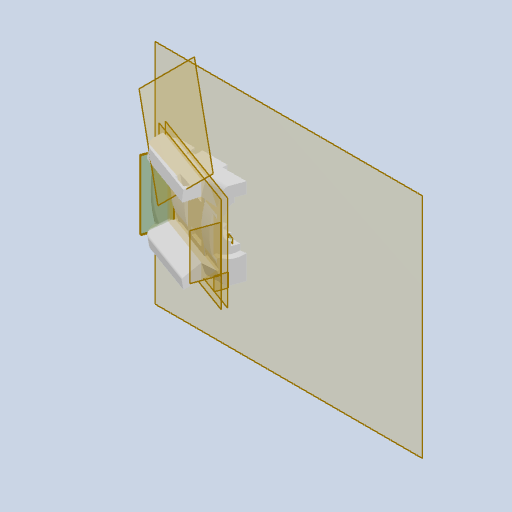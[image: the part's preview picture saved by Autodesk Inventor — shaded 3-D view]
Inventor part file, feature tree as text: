
AUTODESK INVENTOR PART (.ipt)
format: ipt  version: 2022 (Build 260153000, 153)  size: 1,060,352 bytes
history: native  units: mm
features: reference x50, other x25, extrude x24, sketch x23, projected_geometry x12, fillet x11, mirror x2, chamfer x2
ambient origin geometry x8: Origin, YZ Plane, XZ Plane, XY Plane, X Axis, Y Axis, Z Axis, Center Point
bodies: Body1 (feature_tree)
feature tree (149):
  other  "Твердое тело1"
  other  "РабПлоскость1"
  extrude  "Выдавливание1"  Depth=0.3mm
  other  "РабПлоскость2"
  extrude  "Выдавливание2"  Depth=0.3mm
  extrude  "Выдавливание3"  Depth=40.0mm TaperAngle=0.0deg
  other  "РабПлоскость3"
  extrude  "Выдавливание4"  Depth=0.5mm
  extrude  "Выдавливание5"  Depth=0.5mm
  mirror  "Зеркальное отражение1"
  other  "РабПлоскость4"
  extrude  "Выдавливание6"  Depth=0.5mm
  fillet  "Сопряжение1"  Radius=200.0mm
  extrude  "Выдавливание7"  Depth=200.0mm TaperAngle=0.0deg
  extrude  "Выдавливание8"  Depth=1.0mm
  other  "РабПлоскость5"
  extrude  "Выдавливание9"  Depth=10.0mm TaperAngle=0.0deg
  extrude  "Выдавливание10"  Depth=0.2mm
  other  "РабПлоскость6"
  extrude  "Выдавливание11"  Depth=0.2mm
  extrude  "Выдавливание12"  Depth=0.2mm
  chamfer  "Фаска1"  Distance=0.2mm
  extrude  "Выдавливание13"  Depth=17.85mm TaperAngle=0.0deg
  other  "РабПлоскость8"
  extrude  "Выдавливание14"  Depth=17.5mm TaperAngle=0.0deg
  extrude  "Выдавливание15"  Depth=1.675mm TaperAngle=0.0deg
  extrude  "Выдавливание16"  Depth=27.0mm
  fillet  "Сопряжение3"  Radius=1.5mm
  fillet  "Сопряжение4"  Radius=3.15mm
  fillet  "Сопряжение6"  Radius=0.3mm
  extrude  "Выдавливание17"  Depth=200.0mm TaperAngle=0.0deg
  extrude  "Выдавливание18"  Depth=0.4mm
  chamfer  "Фаска2"  Distance=0.4mm
  fillet  "Сопряжение7"  Radius=10.0mm
  extrude  "Выдавливание19"  Depth=1.25mm TaperAngle=0.0deg
  extrude  "Выдавливание20"  Depth=5.0mm TaperAngle=0.0deg
  fillet  "Сопряжение8"  Radius=0.8mm
  fillet  "Сопряжение9"  Radius=10.0mm
  other  "РабПлоскость9"
  extrude  "Выдавливание21"  Depth=5.0mm TaperAngle=0.0deg
  extrude  "Выдавливание22"  Depth=10.0mm TaperAngle=0.0deg
  fillet  "Сопряжение10"  Radius=1.5mm
  mirror  "Зеркальное отражение2"
  fillet  "Сопряжение11"  Radius=4.2mm
  extrude  "Выдавливание23"  Depth=4.2mm
  fillet  "Сопряжение12"  Radius=7.0mm
  fillet  "Сопряжение13"  [1 undecoded]
  extrude  "Выдавливание24"  Depth=10.0mm TaperAngle=0.0deg
  sketch  "Эскиз2"
  reference  "Ссылка7"
  reference  "Ссылка8"
  reference  "Ссылка9"
  sketch  "Эскиз3"
  reference  "Ссылка10"
  reference  "Ссылка11"
  reference  "Ссылка12"
  reference  "Ссылка13"
  reference  "Ссылка14"
  reference  "Ссылка15"
  reference  "Ссылка16"
  reference  "Ссылка17"
  reference  "Ссылка18"
  sketch  "Эскиз4"
  reference  "Ссылка19"
  reference  "Ссылка20"
  reference  "Ссылка21"
  projected_geometry  "Спроецированная петля1"
  projected_geometry  "Спроецированная петля2"
  projected_geometry  "Спроецированная петля3"
  projected_geometry  "Спроецированная петля4"
  sketch  "Эскиз5"
  reference  "Ссылка22"
  sketch  "Эскиз6"
  reference  "Ссылка23"
  reference  "Ссылка24"
  reference  "Ссылка25"
  reference  "Ссылка26"
  reference  "Ссылка27"
  reference  "Ссылка28"
  reference  "Ссылка29"
  sketch  "Эскиз7"
  reference  "Ссылка30"
  projected_geometry  "Спроецированная петля5"
  sketch  "Эскиз8"
  sketch  "Эскиз9"
  reference  "Ссылка31"
  sketch  "Эскиз10"
  reference  "Ссылка32"
  reference  "Ссылка33"
  sketch  "Эскиз11"
  reference  "Ссылка34"
  reference  "Ссылка35"
  sketch  "Эскиз12"
  projected_geometry  "Спроецированная петля6"
  projected_geometry  "Спроецированная петля7"
  sketch  "Эскиз13"
  projected_geometry  "Спроецированная петля8"
  other  "РабПлоскость7"
  sketch  "Эскиз15"
  sketch  "Эскиз16"
  projected_geometry  "Спроецированная петля9"
  sketch  "Эскиз17"
  reference  "Ссылка36"
  reference  "Ссылка37"
  reference  "Ссылка38"
  reference  "Ссылка39"
  reference  "Ссылка40"
  reference  "Ссылка41"
  reference  "Ссылка42"
  reference  "Ссылка43"
  sketch  "Эскиз18"
  sketch  "Эскиз19"
  reference  "Ссылка44"
  reference  "Ссылка45"
  sketch  "Эскиз20"
  reference  "Ссылка46"
  projected_geometry  "Спроецированная петля10"
  reference  "Ссылка47"
  sketch  "Эскиз21"
  projected_geometry  "Спроецированная петля11"
  reference  "Ссылка48"
  reference  "Ссылка49"
  sketch  "Эскиз22"
  reference  "Ссылка50"
  sketch  "Эскиз23"
  reference  "Ссылка51"
  reference  "Ссылка52"
  reference  "Ссылка53"
  sketch  "Эскиз24"
  projected_geometry  "Спроецированная петля12"
  sketch  "Эскиз25"
  reference  "Ссылка54"
  reference  "Ссылка55"
  reference  "Ссылка56"
  other  "<userpath>\Documents\Git\MZCAT_2024_construction\MZCAT_2024_RPI_2\MZCAT_4.iam"
  other  "MZCAT_4.iam"
  other  "CAT_protector:1"
  other  "vydacha_slide:1"
  other  "<userpath>\Documents\Git\MZCAT_2024\MZCAT_4.iam"
  other  "magazine:1"
  other  "vydacha_pusher:1"
  other  "OCS-D008 B:1"
  other  "back_diffuser:1"
  other  "back_led_board:1"
  other  "left_back_cup:1"
  other  "antenna:2"
  other  "MZCAT_backlight_board:1"
  other  "<userpath>\Documents\Git\MZCAT_2024\MZCAT_3.iam"
  other  "MZCAT_3.iam"
note: 1 required parameter value undecoded (feature->parameter linkage not recoverable at this tier; creation-order binding heuristic only, values carry confidence <= 0.55)
